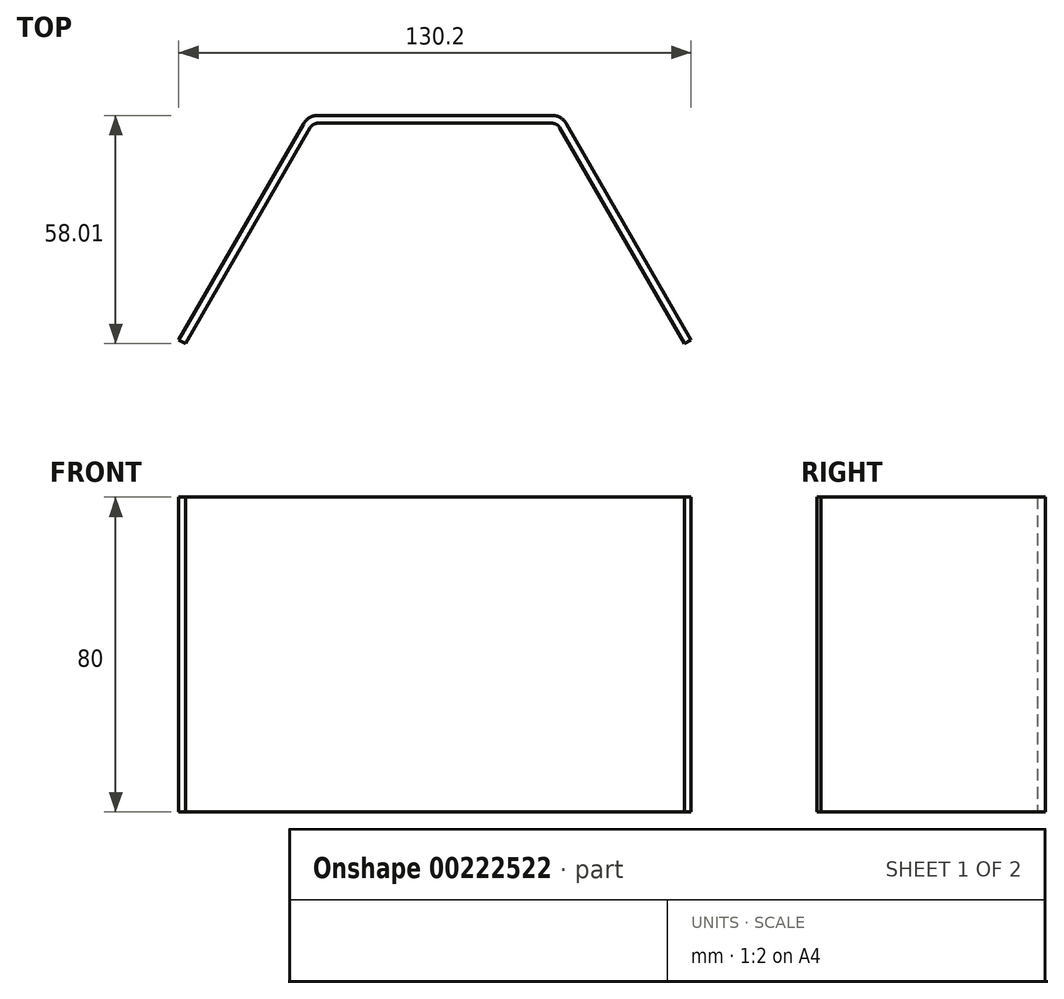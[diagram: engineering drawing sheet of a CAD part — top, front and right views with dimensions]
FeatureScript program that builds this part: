
annotation { "Feature Type Name" : "Feature", "Feature Type Description" : "" }
export const myFeature = defineFeature(function(context is Context, id is Id, definition is map)
    precondition{}
    {
        {
            var Q0;
            Q0=qCreatedBy(makeId("Top.planeOp"),FACE);
            var sketch = newSketch(context, id + "F0", { "sketchPlane" : qUnion([Q0])});
            skLineSegment(sketch, "E0", {"start": v(-31.68, 21.63) * mm, "end": v(27.72, 21.63) * mm});
            skLineSegment(sketch, "E1", {"start": v(-33.67, 20.48) * mm, "end": v(-65.35, -34.38) * mm});
            skLineSegment(sketch, "E2", {"start": v(29.71, 20.48) * mm, "end": v(61.39, -34.38) * mm});
            skPoint(sketch, "E3.visualSharp", {"position": v(-33, 21.63) * mm});
            skArc(sketch, "E3.filletArc", {"start": v(-31.68, 21.63) * mm, "mid": v(-32.83, 21.33) * mm, "end": v(-33.67, 20.48) * mm});
            skPoint(sketch, "E4.visualSharp", {"position": v(29.05, 21.63) * mm});
            skArc(sketch, "E4.filletArc", {"start": v(29.71, 20.48) * mm, "mid": v(28.87, 21.33) * mm, "end": v(27.72, 21.63) * mm});
            skLineSegment(sketch, "E5.0", {"start": v(31.44, 21.48) * mm, "end": v(63.12, -33.38) * mm});
            skLineSegment(sketch, "E5.1", {"start": v(-35.4, 21.48) * mm, "end": v(-67.08, -33.38) * mm});
            skArc(sketch, "E5.2", {"start": v(-31.68, 23.63) * mm, "mid": v(-33.83, 23.06) * mm, "end": v(-35.4, 21.48) * mm});
            skLineSegment(sketch, "E5.3", {"start": v(-31.68, 23.63) * mm, "end": v(27.72, 23.63) * mm});
            skArc(sketch, "E5.4", {"start": v(31.44, 21.48) * mm, "mid": v(29.87, 23.06) * mm, "end": v(27.72, 23.63) * mm});
            skLineSegment(sketch, "E6", {"start": v(-67.08, -33.38) * mm, "end": v(-65.35, -34.38) * mm});
            skLineSegment(sketch, "E7", {"start": v(63.12, -33.38) * mm, "end": v(61.39, -34.38) * mm});
            skSolve(sketch);
        }
        {
            var Q0;
            Q0 = qSketchRegion(id + "F0", true);
            extrude(context, id + "F1", {"entities" : qUnion([Q0]), "depth" : 80 * mm});
        }
    });
